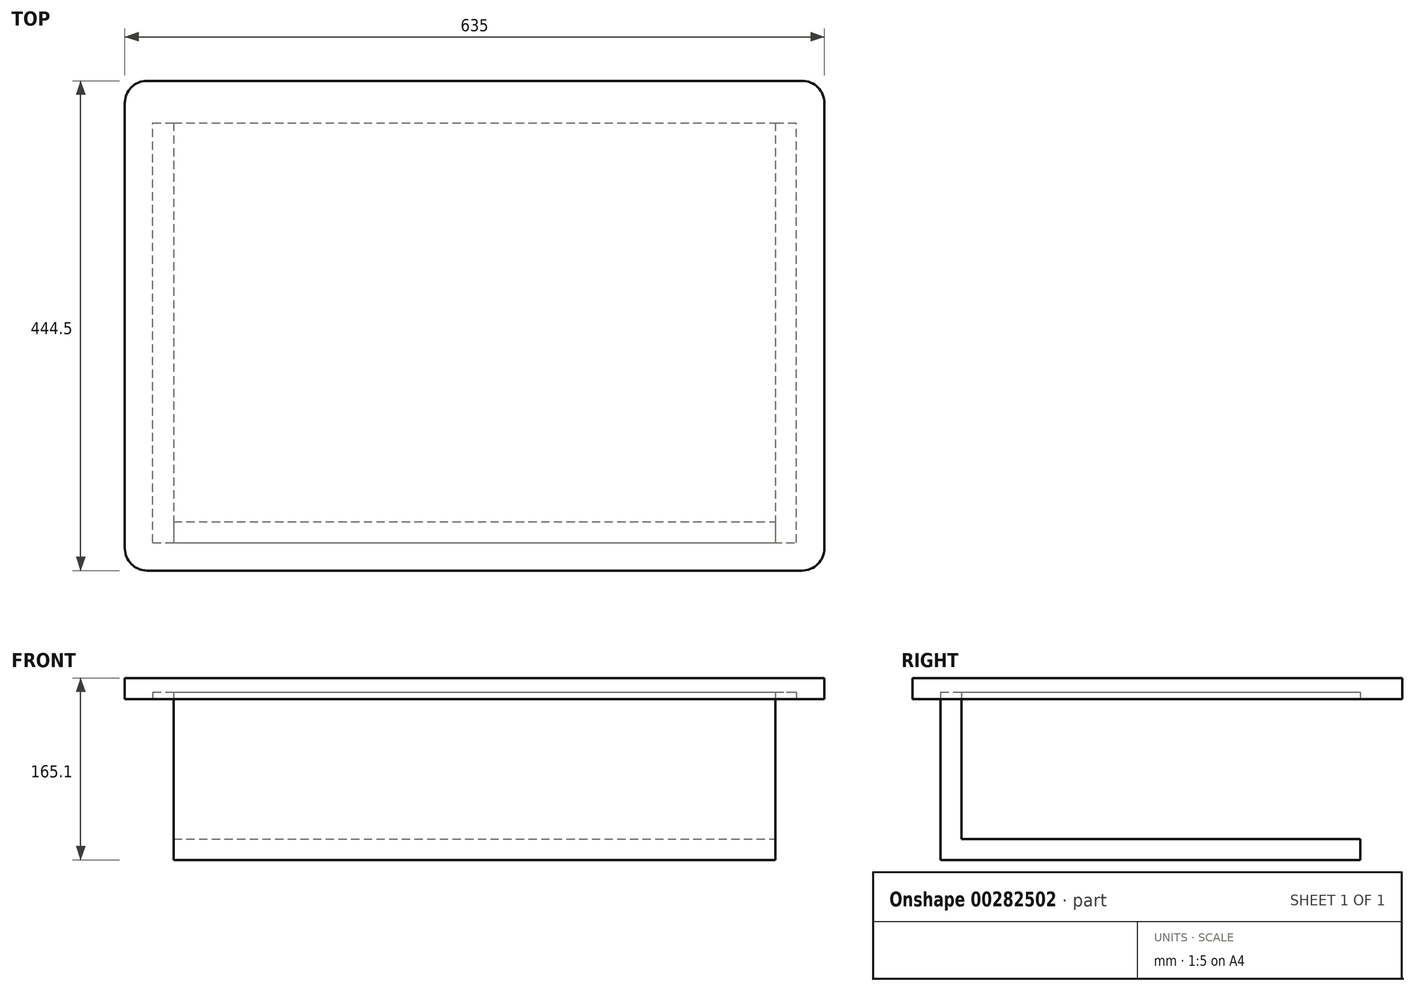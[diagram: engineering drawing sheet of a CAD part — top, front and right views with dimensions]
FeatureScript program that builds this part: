
annotation { "Feature Type Name" : "Feature", "Feature Type Description" : "" }
export const myFeature = defineFeature(function(context is Context, id is Id, definition is map)
    precondition{}
    {
        {
            var Q0;
            Q0=qCreatedBy(makeId("Top.planeOp"),FACE);
            var sketch = newSketch(context, id + "F0", { "sketchPlane" : qUnion([Q0])});
            skLineSegment(sketch, "E0.bottom", {"start": v(-296.8, 242.15) * mm, "end": v(297.55, 242.15) * mm});
            skLineSegment(sketch, "E0.top", {"start": v(-296.8, -202.35) * mm, "end": v(297.55, -202.35) * mm});
            skLineSegment(sketch, "E0.left", {"start": v(-317.13, 221.83) * mm, "end": v(-317.13, -182.03) * mm});
            skLineSegment(sketch, "E0.right", {"start": v(317.87, 221.83) * mm, "end": v(317.87, -182.03) * mm});
            skPoint(sketch, "E0.middle", {"position": v(0.37, 19.9) * mm});
            skPoint(sketch, "E1.visualSharp", {"position": v(-317.13, 242.15) * mm});
            skArc(sketch, "E1.filletArc", {"start": v(-296.8, 242.15) * mm, "mid": v(-311.18, 236.2) * mm, "end": v(-317.13, 221.83) * mm});
            skPoint(sketch, "E2.visualSharp", {"position": v(-317.13, -202.35) * mm});
            skArc(sketch, "E2.filletArc", {"start": v(-317.13, -182.03) * mm, "mid": v(-311.18, -196.4) * mm, "end": v(-296.8, -202.35) * mm});
            skPoint(sketch, "E3.visualSharp", {"position": v(317.87, -202.35) * mm});
            skArc(sketch, "E3.filletArc", {"start": v(297.55, -202.35) * mm, "mid": v(311.92, -196.4) * mm, "end": v(317.87, -182.03) * mm});
            skPoint(sketch, "E4.visualSharp", {"position": v(317.87, 242.15) * mm});
            skArc(sketch, "E4.filletArc", {"start": v(317.87, 221.83) * mm, "mid": v(311.92, 236.2) * mm, "end": v(297.55, 242.15) * mm});
            skSolve(sketch);
        }
        {
            var Q0;
            Q0=qSketchRegion(id+"F0",true);
            extrude(context, id + "F1", {"entities" : qUnion([Q0]), "depth" : 19.05 * mm});
        }
        {
            var Q0;
            Q0=makeQuery(id+"F1.opExtrude","CAP_FACE",FACE,{"disambiguationData":[OSD([sQuery(id+"F0.wireOp",EDGE,"E0.bottom"),sQuery(id+"F0.wireOp",EDGE,"E0.top"),sQuery(id+"F0.wireOp",EDGE,"E0.left"),sQuery(id+"F0.wireOp",EDGE,"E0.right"),sQuery(id+"F0.wireOp",EDGE,"E1.filletArc"),sQuery(id+"F0.wireOp",EDGE,"E2.filletArc"),sQuery(id+"F0.wireOp",EDGE,"E3.filletArc"),sQuery(id+"F0.wireOp",EDGE,"E4.filletArc")])],"isStart":true});
            var sketch = newSketch(context, id + "F2", { "sketchPlane" : qUnion([Q0])});
            skLineSegment(sketch, "E5.bottom", {"start": v(-291.73, 176.95) * mm, "end": v(-272.68, 176.95) * mm});
            skLineSegment(sketch, "E5.top", {"start": v(-291.73, -204.05) * mm, "end": v(-272.68, -204.05) * mm});
            skLineSegment(sketch, "E5.left", {"start": v(-291.73, 176.95) * mm, "end": v(-291.73, -204.05) * mm});
            skLineSegment(sketch, "E5.right", {"start": v(-272.68, 176.95) * mm, "end": v(-272.68, -204.05) * mm});
            skSolve(sketch);
        }
        {
            var Q0;
            Q0=qSketchRegion(id+"F2",true);
            extrude(context, id + "F3", {"entities" : qUnion([Q0]), "operationType" : NewBodyOperationType.REMOVE, "oppositeDirection" : true, "depth" : 6.35 * mm});
        }
        {
            var Q0;
            Q0=makeQuery(id+"F1.opExtrude","CAP_FACE",FACE,{"disambiguationData":[OSD([sQuery(id+"F0.wireOp",EDGE,"E0.bottom"),sQuery(id+"F0.wireOp",EDGE,"E0.top"),sQuery(id+"F0.wireOp",EDGE,"E0.left"),sQuery(id+"F0.wireOp",EDGE,"E0.right"),sQuery(id+"F0.wireOp",EDGE,"E1.filletArc"),sQuery(id+"F0.wireOp",EDGE,"E2.filletArc"),sQuery(id+"F0.wireOp",EDGE,"E3.filletArc"),sQuery(id+"F0.wireOp",EDGE,"E4.filletArc")])],"isStart":true});
            var sketch = newSketch(context, id + "F4", { "sketchPlane" : qUnion([Q0])});
            skLineSegment(sketch, "E6.bottom", {"start": v(-272.68, 176.95) * mm, "end": v(273.42, 176.95) * mm});
            skLineSegment(sketch, "E6.top", {"start": v(-272.68, 157.9) * mm, "end": v(273.42, 157.9) * mm});
            skLineSegment(sketch, "E6.left", {"start": v(-272.68, 176.95) * mm, "end": v(-272.68, 157.9) * mm});
            skLineSegment(sketch, "E6.right", {"start": v(273.42, 176.95) * mm, "end": v(273.42, 157.9) * mm});
            skSolve(sketch);
        }
        {
            var Q0;
            Q0=qSketchRegion(id+"F4",true);
            extrude(context, id + "F5", {"entities" : qUnion([Q0]), "operationType" : NewBodyOperationType.REMOVE, "oppositeDirection" : true, "depth" : 6.35 * mm});
        }
        {
            var Q0;
            Q0=makeQuery(id+"F1.opExtrude","CAP_FACE",FACE,{"disambiguationData":[OSD([sQuery(id+"F0.wireOp",EDGE,"E0.bottom"),sQuery(id+"F0.wireOp",EDGE,"E0.top"),sQuery(id+"F0.wireOp",EDGE,"E0.left"),sQuery(id+"F0.wireOp",EDGE,"E0.right"),sQuery(id+"F0.wireOp",EDGE,"E1.filletArc"),sQuery(id+"F0.wireOp",EDGE,"E2.filletArc"),sQuery(id+"F0.wireOp",EDGE,"E3.filletArc"),sQuery(id+"F0.wireOp",EDGE,"E4.filletArc")])],"isStart":true});
            var sketch = newSketch(context, id + "F6", { "sketchPlane" : qUnion([Q0])});
            skLineSegment(sketch, "E7.bottom", {"start": v(273.42, 176.95) * mm, "end": v(292.47, 176.95) * mm});
            skLineSegment(sketch, "E7.top", {"start": v(273.42, -204.05) * mm, "end": v(292.47, -204.05) * mm});
            skLineSegment(sketch, "E7.left", {"start": v(273.42, 176.95) * mm, "end": v(273.42, -204.05) * mm});
            skLineSegment(sketch, "E7.right", {"start": v(292.47, 176.95) * mm, "end": v(292.47, -204.05) * mm});
            skSolve(sketch);
        }
        {
            var Q0;
            Q0=qSketchRegion(id+"F6",true);
            extrude(context, id + "F7", {"entities" : qUnion([Q0]), "operationType" : NewBodyOperationType.REMOVE, "oppositeDirection" : true, "depth" : 6.35 * mm});
        }
        {
            var Q0;
            Q0=makeQuery(id+"F1.opExtrude","CAP_FACE",FACE,{"disambiguationData":[OSD([sQuery(id+"F0.wireOp",EDGE,"E0.bottom"),sQuery(id+"F0.wireOp",EDGE,"E0.top"),sQuery(id+"F0.wireOp",EDGE,"E0.left"),sQuery(id+"F0.wireOp",EDGE,"E0.right"),sQuery(id+"F0.wireOp",EDGE,"E1.filletArc"),sQuery(id+"F0.wireOp",EDGE,"E2.filletArc"),sQuery(id+"F0.wireOp",EDGE,"E3.filletArc"),sQuery(id+"F0.wireOp",EDGE,"E4.filletArc")])],"isStart":true});
            var sketch = newSketch(context, id + "F8", { "sketchPlane" : qUnion([Q0])});
            skLineSegment(sketch, "E8.bottom", {"start": v(-272.68, 157.9) * mm, "end": v(273.42, 157.9) * mm});
            skLineSegment(sketch, "E8.top", {"start": v(-272.68, 176.95) * mm, "end": v(273.42, 176.95) * mm});
            skLineSegment(sketch, "E8.left", {"start": v(-272.68, 157.9) * mm, "end": v(-272.68, 176.95) * mm});
            skLineSegment(sketch, "E8.right", {"start": v(273.42, 157.9) * mm, "end": v(273.42, 176.95) * mm});
            skSolve(sketch);
        }
        {
            var Q0;
            Q0=qSketchRegion(id+"F8",true);
            extrude(context, id + "F9", {"entities" : qUnion([Q0]), "depth" : 127 * mm});
        }
        {
            var Q0;
            Q0=makeQuery(id+"F9.opExtrude","CAP_FACE",FACE,{"disambiguationData":[OSD([sQuery(id+"F8.wireOp",EDGE,"E8.bottom"),sQuery(id+"F8.wireOp",EDGE,"E8.top"),sQuery(id+"F8.wireOp",EDGE,"E8.left"),sQuery(id+"F8.wireOp",EDGE,"E8.right")])],"isStart":false});
            var sketch = newSketch(context, id + "F10", { "sketchPlane" : qUnion([Q0])});
            skLineSegment(sketch, "E9.bottom", {"start": v(-272.68, 176.95) * mm, "end": v(273.42, 176.95) * mm});
            skLineSegment(sketch, "E9.top", {"start": v(-272.68, -204.05) * mm, "end": v(273.42, -204.05) * mm});
            skLineSegment(sketch, "E9.left", {"start": v(-272.68, 176.95) * mm, "end": v(-272.68, -204.05) * mm});
            skLineSegment(sketch, "E9.right", {"start": v(273.42, 176.95) * mm, "end": v(273.42, -204.05) * mm});
            skSolve(sketch);
        }
        {
            var Q0;
            Q0=qSketchRegion(id+"F10",true);
            extrude(context, id + "F11", {"entities" : qUnion([Q0]), "operationType" : NewBodyOperationType.ADD, "depth" : 19.05 * mm});
        }
    });
